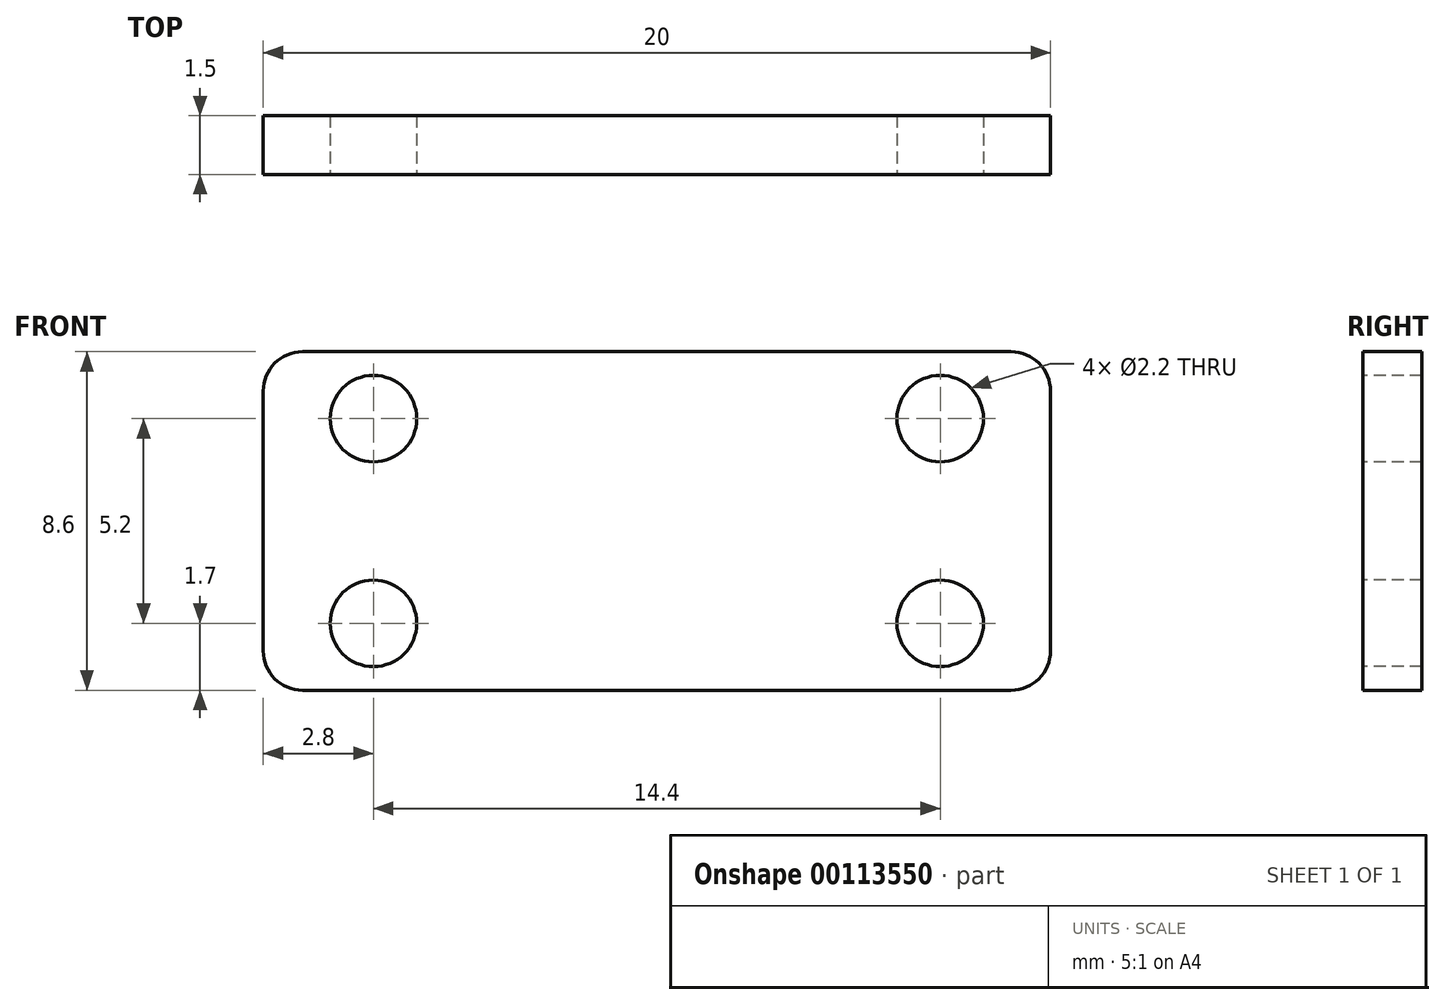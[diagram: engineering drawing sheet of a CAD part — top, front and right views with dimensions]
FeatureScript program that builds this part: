
annotation { "Feature Type Name" : "Feature", "Feature Type Description" : "" }
export const myFeature = defineFeature(function(context is Context, id is Id, definition is map)
    precondition{}
    {
        {
            var Q0;
            Q0=qCreatedBy(makeId("Front.planeOp"),FACE);
            var sketch = newSketch(context, id + "F0", { "sketchPlane" : qUnion([Q0])});
            skLineSegment(sketch, "E0.bottom", {"start": v(0, 0) * mm, "end": v(20, 0) * mm});
            skLineSegment(sketch, "E0.top", {"start": v(0, 8.6) * mm, "end": v(20, 8.6) * mm});
            skLineSegment(sketch, "E0.left", {"start": v(0, 0) * mm, "end": v(0, 8.6) * mm});
            skLineSegment(sketch, "E0.right", {"start": v(20, 0) * mm, "end": v(20, 8.6) * mm});
            skSolve(sketch);
        }
        {
            var Q0;
            Q0=qSketchRegion(id+"F0",true);
            extrude(context, id + "F1", {"entities" : qUnion([Q0]), "depth" : 1.5 * mm});
        }
        {
            var Q0;
            Q0=makeQuery(id+"F1.opExtrude","CAP_FACE",FACE,{"disambiguationData":[OSD([sQuery(id+"F0.wireOp",EDGE,"E0.bottom"),sQuery(id+"F0.wireOp",EDGE,"E0.top"),sQuery(id+"F0.wireOp",EDGE,"E0.left"),sQuery(id+"F0.wireOp",EDGE,"E0.right")])],"isStart":false});
            var sketch = newSketch(context, id + "F2", { "sketchPlane" : qUnion([Q0])});
            skLineSegment(sketch, "E1", {"start": v(0, 4.3) * mm, "end": v(20, 4.3) * mm, "construction": true});
            skLineSegment(sketch, "E2", {"start": v(10, 8.6) * mm, "end": v(10, 0) * mm, "construction": true});
            skPoint(sketch, "E3", {"position": v(10, 4.3) * mm});
            skCircle(sketch, "E4", {"center": v(2.8, 6.9) * mm, "radius": 1.1 * mm});
            skCircle(sketch, "E5.MirrorC", {"center": v(17.2, 6.9) * mm, "radius": 1.1 * mm});
            skCircle(sketch, "E6.MirrorC", {"center": v(2.8, 1.7) * mm, "radius": 1.1 * mm});
            skCircle(sketch, "E7.MirrorC", {"center": v(17.2, 1.7) * mm, "radius": 1.1 * mm});
            skSolve(sketch);
        }
        {
            var Q0;
            Q0=qSketchRegion(id+"F2",true);
            extrude(context, id + "F3", {"entities" : qUnion([Q0]), "operationType" : NewBodyOperationType.REMOVE, "endBound" : BoundingType.UP_TO_NEXT, "oppositeDirection" : true, "depth" : 25 * mm});
        }
        {
            var Q0;
            Q0=makeQuery(id+"F1.opExtrude","SWEPT_EDGE",EDGE,{"disambiguationData":[OSD([sQuery(id+"F0.wireOp",EDGE,"E0.top"),sQuery(id+"F0.wireOp",EDGE,"E0.right")])]});
            var Q1;
            Q1=makeQuery(id+"F1.opExtrude","SWEPT_EDGE",EDGE,{"disambiguationData":[OSD([sQuery(id+"F0.wireOp",EDGE,"E0.bottom"),sQuery(id+"F0.wireOp",EDGE,"E0.right")])]});
            var Q2;
            Q2=makeQuery(id+"F1.opExtrude","SWEPT_EDGE",EDGE,{"disambiguationData":[OSD([sQuery(id+"F0.wireOp",EDGE,"E0.top"),sQuery(id+"F0.wireOp",EDGE,"E0.left")])]});
            var Q3;
            Q3=makeQuery(id+"F1.opExtrude","SWEPT_EDGE",EDGE,{"disambiguationData":[OSD([sQuery(id+"F0.wireOp",EDGE,"E0.bottom"),sQuery(id+"F0.wireOp",EDGE,"E0.left")])]});
            fillet(context, id + "F4", {"entities" : qUnion([Q0, Q1, Q2, Q3]), "radius" : 1 * mm, "tangentPropagation" : true, "allowEdgeOverflow" : false});
        }
    });
